# Revit family: Plumbing_Other_hansgrohe_40917007-Hansgrohe-POE-BWF-82-S20-backwa_
name_source: partatom
category: Plumbing Fixtures
revit_build: Autodesk Revit 2015 (Build: 20140903_1530(x64)
units: mm (PartAtom-declared; Revit-internal decimal feet)

## types (1)
- n.a.
    BIMobject category = Other
    BIMobject category code = plumbing-other
    BIMobject main category = Plumbing
    BIMobject main category code = plumbing
    BOSUseNativeGeometries = 1
    Brand url = http://www.hansgrohe-int.com
    Default Elevation = 4' - 0"
    Design country = Germany
    Edition number = 1
    GTIN code = https://4059625191880
    IFC Classification = Sanitary Terminal
    Manufacturer country = Germany
    Manufacturer name = hansgrohe
    Masterformat 2014 Code = 12 58 00
    Masterformat 2014 Description = Residential Furniture
    Material main = Plastic
    Material secondary = Plastic
    NBS Reference Code = 31-75
    NBS Reference Description = Sanitary Accessories
    Product Guid = b2dcbcdb-bce4-485a-8082-ffffd4536f31
    Product SKU = 40917007
    Product data url = https://bimobject.com
    Product family = hansgrohe
    Product group = Filtration
    Product name = 40917007 Hansgrohe POE BWF 82-S20 backwash filter
    QR code = http://bimobject.com
    UNSPSC Code = 3018
    Uniclass 1.4 Code = L721
    Uniclass 1.4 Description = Sanitary equipment
    Uniclass 2.0 Code = PR-31-75
    Uniclass 2.0 Description = Sanitary Accessories
    Uniformat II Code = D2010
    Uniformat II Description = Plumbing Fixtures

## geometry (parser evidence)
native form markers: Sweep x2
no freeform markers — native parametric forms only
